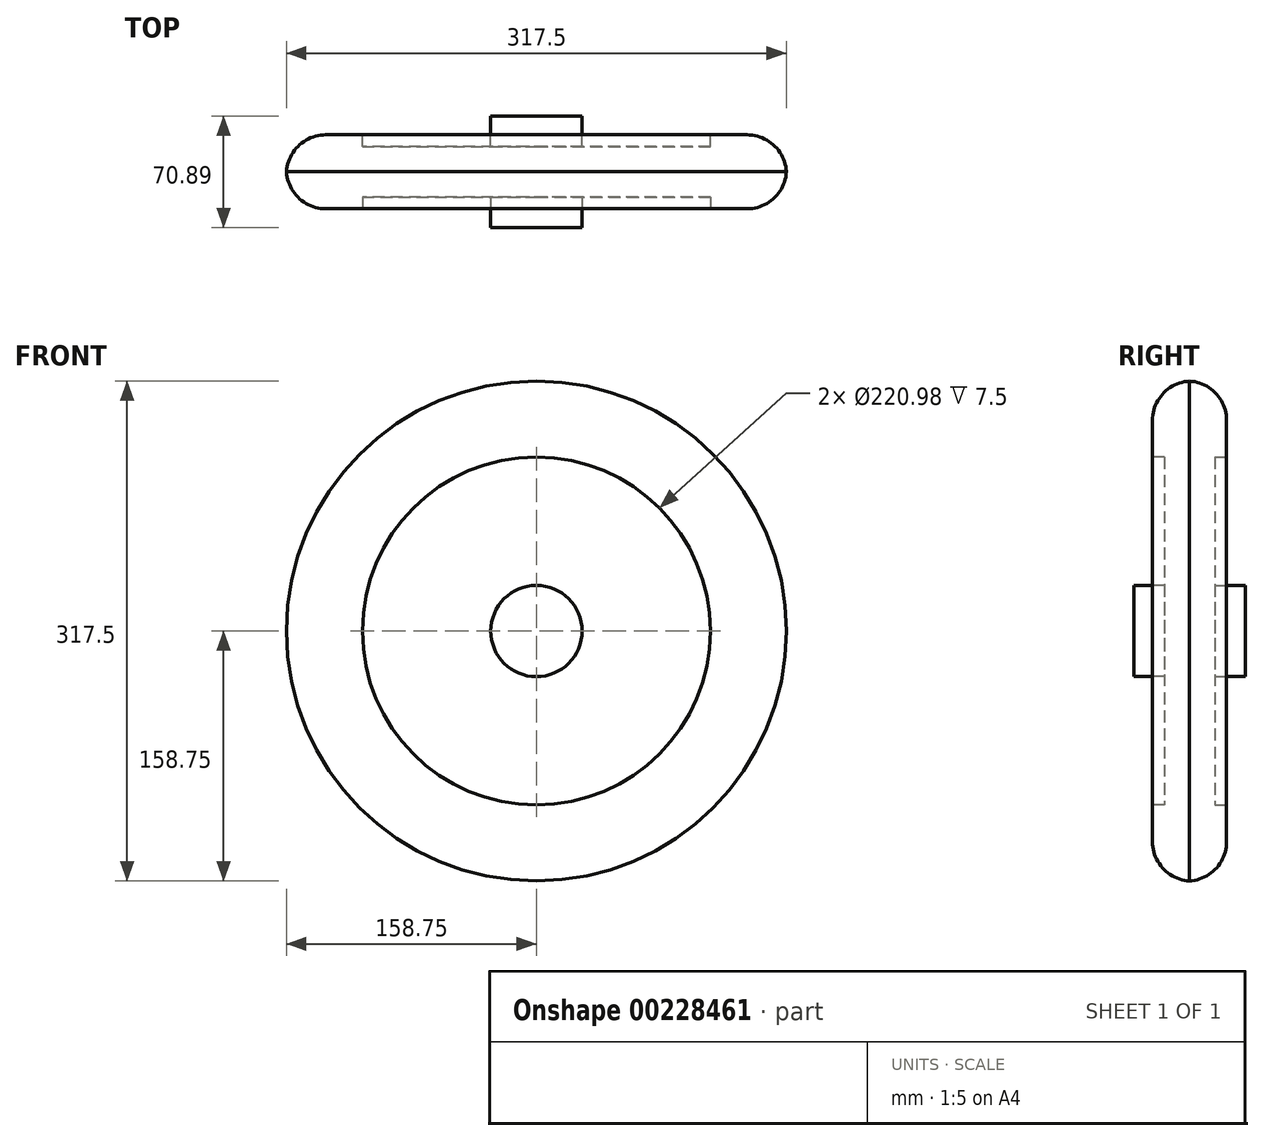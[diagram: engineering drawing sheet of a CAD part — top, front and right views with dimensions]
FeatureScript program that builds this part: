
annotation { "Feature Type Name" : "Feature", "Feature Type Description" : "" }
export const myFeature = defineFeature(function(context is Context, id is Id, definition is map)
    precondition{}
    {
        {
            var Q0;
            Q0=qCreatedBy(makeId("Front.planeOp"),FACE);
            var sketch = newSketch(context, id + "F0", { "sketchPlane" : qUnion([Q0])});
            skCircle(sketch, "E0", {"center": v(0, 0) * mm, "radius": 158.75 * mm});
            skSolve(sketch);
        }
        {
            var Q0;
            Q0 = qSketchRegion(id + "F0", true);
            extrude(context, id + "F1", {"entities" : qUnion([Q0]), "depth" : 47 * mm / 2});
        }
        {
            var Q0;
            Q0=makeQuery(id+"F1.opExtrude","CAP_EDGE",EDGE,{"disambiguationData":[OSD([sQuery(id+"F0.wireOp",EDGE,"E0")])],"isStart":true});
            fillet(context, id + "F2", {"entities" : qUnion([Q0]), "radius" : 25 * mm, "tangentPropagation" : true, "allowEdgeOverflow" : false});
        }
        {
            var Q0;
            Q0=makeQuery(id+"F1.opExtrude","CAP_FACE",FACE,{"disambiguationData":[OSD([sQuery(id+"F0.wireOp",EDGE,"E0")])],"isStart":true});
            var sketch = newSketch(context, id + "F3", { "sketchPlane" : qUnion([Q0])});
            skCircle(sketch, "E1", {"center": v(0, 0) * mm, "radius": 110.5 * mm});
            skCircle(sketch, "E2", {"center": v(0, 0) * mm, "radius": 29 * mm});
            skSolve(sketch);
        }
        {
            var Q0;
            Q0 = qSketchRegion(id + "F3", true);
            extrude(context, id + "F4", {"entities" : qUnion([Q0]), "operationType" : NewBodyOperationType.REMOVE, "oppositeDirection" : true, "depth" : 7.5 * mm});
        }
        {
            var Q0;
            Q0=makeQuery(id+"F4.boolean.opBoolean","SPLIT",FACE,{"disambiguationData":[TD([makeQuery(id+"F4.opExtrude","SWEPT_FACE",FACE,{"disambiguationData":[OSD([sQuery(id+"F3.wireOp",EDGE,"E2")])]})])],"derivedFrom":makeQuery(id+"F1.opExtrude","CAP_FACE",FACE,{"disambiguationData":[OSD([sQuery(id+"F0.wireOp",EDGE,"E0")])],"isStart":true})});
            extrude(context, id + "F5", {"entities" : qUnion([Q0]), "operationType" : NewBodyOperationType.ADD, "depth" : 11.95 * mm});
        }
        {
            var Q0;
            Q0=makeQuery(id+"F1.opExtrude","SWEPT_BODY",BODY,{"disambiguationData":[OSD([sQuery(id+"F0.wireOp",EDGE,"E0")])]});
            var Q1;
            Q1=makeQuery(id+"F1.opExtrude","CAP_FACE",FACE,{"disambiguationData":[OSD([sQuery(id+"F0.wireOp",EDGE,"E0")])],"isStart":false});
            mirror(context, id + "F6", {"operationType" : NewBodyOperationType.ADD, "entities" : qUnion([Q0]), "mirrorPlane" : qUnion([Q1])});
        }
    });
